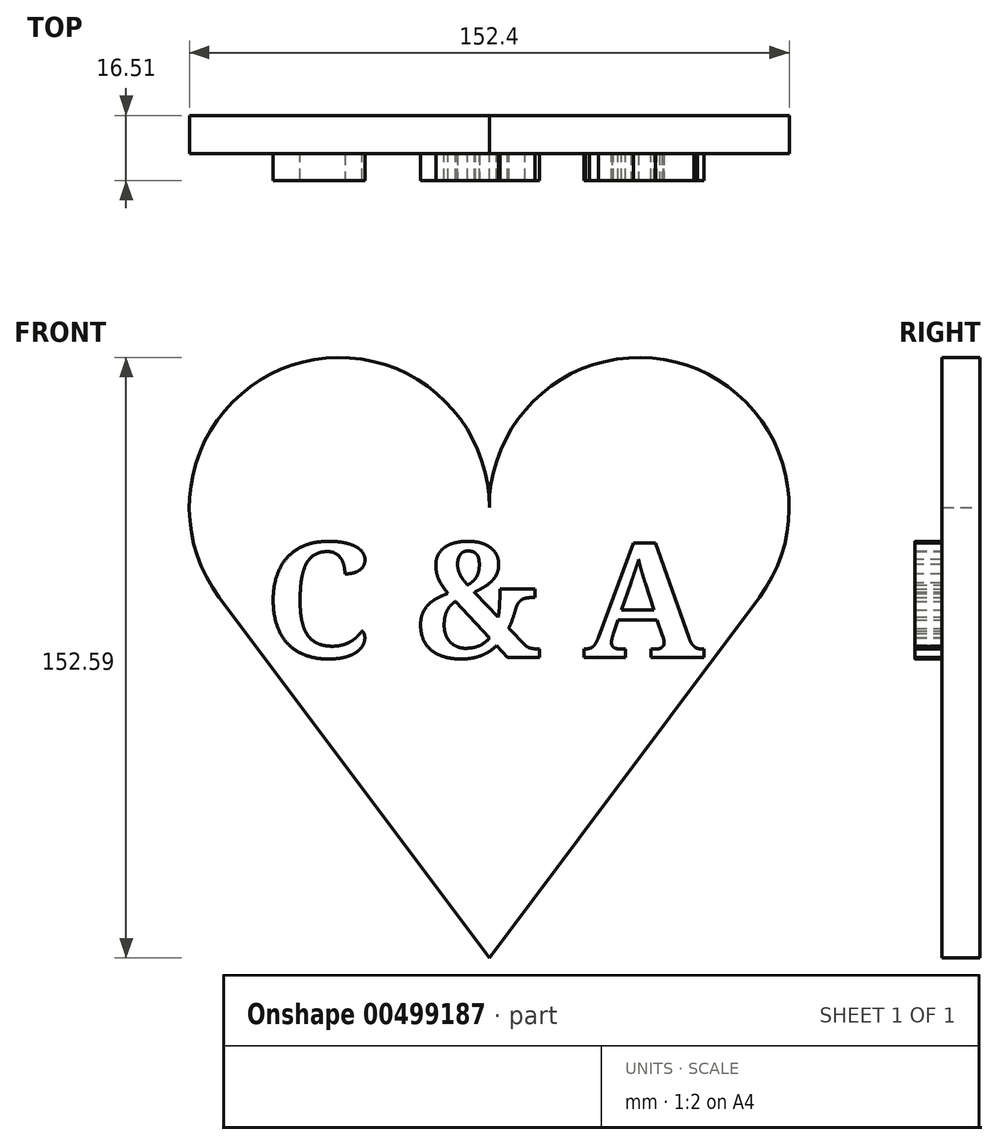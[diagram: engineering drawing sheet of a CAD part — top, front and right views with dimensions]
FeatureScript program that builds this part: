
annotation { "Feature Type Name" : "Feature", "Feature Type Description" : "" }
export const myFeature = defineFeature(function(context is Context, id is Id, definition is map)
    precondition{}
    {
        {
            var Q0;
            Q0=qCreatedBy(makeId("Front.planeOp"),FACE);
            var sketch = newSketch(context, id + "F0", { "sketchPlane" : qUnion([Q0])});
            skCircle(sketch, "E0", {"center": v(-38.1, 38.1) * mm, "radius": 38.1 * mm});
            skCircle(sketch, "E1", {"center": v(38.1, 38.1) * mm, "radius": 38.1 * mm});
            skLineSegment(sketch, "E2", {"start": v(-68.6, 15.27) * mm, "end": v(0, -76.39) * mm});
            skLineSegment(sketch, "E3", {"start": v(0, -76.39) * mm, "end": v(68.6, 15.27) * mm});
            skSolve(sketch);
        }
        {
            var Q0;
            Q0 = qSketchRegion(id + "F0", true);
            extrude(context, id + "F1", {"entities" : qUnion([Q0]), "depth" : 9.65 * mm});
        }
        {
            var Q0;
            Q0=makeQuery(id+"F1.opExtrude","CAP_FACE",FACE,{"disambiguationData":[OSD([sQuery(id+"F0.wireOp",EDGE,"E0"),sQuery(id+"F0.wireOp",EDGE,"E1"),sQuery(id+"F0.wireOp",EDGE,"E2"),sQuery(id+"F0.wireOp",EDGE,"E3")])],"isStart":false});
            var sketch = newSketch(context, id + "F2", { "sketchPlane" : qUnion([Q0])});
            skText(sketch, "E4", { "text": "C & A", "fontName": "NotoSerif-Bold.ttf"});
            const initialGuessF2  = {"E4": [-0.05715, 0, 1, 0, 0.02933]};
            skSetInitialGuess(sketch, initialGuessF2);
            skSolve(sketch);
        }
        {
            var Q0;
            Q0=makeQuery(id+"F2.imprint","IMPRINT",FACE,{"disambiguationData":[TD([[makeQuery(id+"F2.imprint","IMPRINT",EDGE,{"derivedFrom":sQuery(id+"F2.wireOp",EDGE,"E4.sketch_text.stroke-38")}),-1.0]])]});
            var Q1;
            Q1 = qSketchRegion(id + "F2", true);
            extrude(context, id + "F3", {"entities" : qUnion([Q0, Q1]), "operationType" : NewBodyOperationType.ADD, "depth" : 6.86 * mm});
        }
    });
